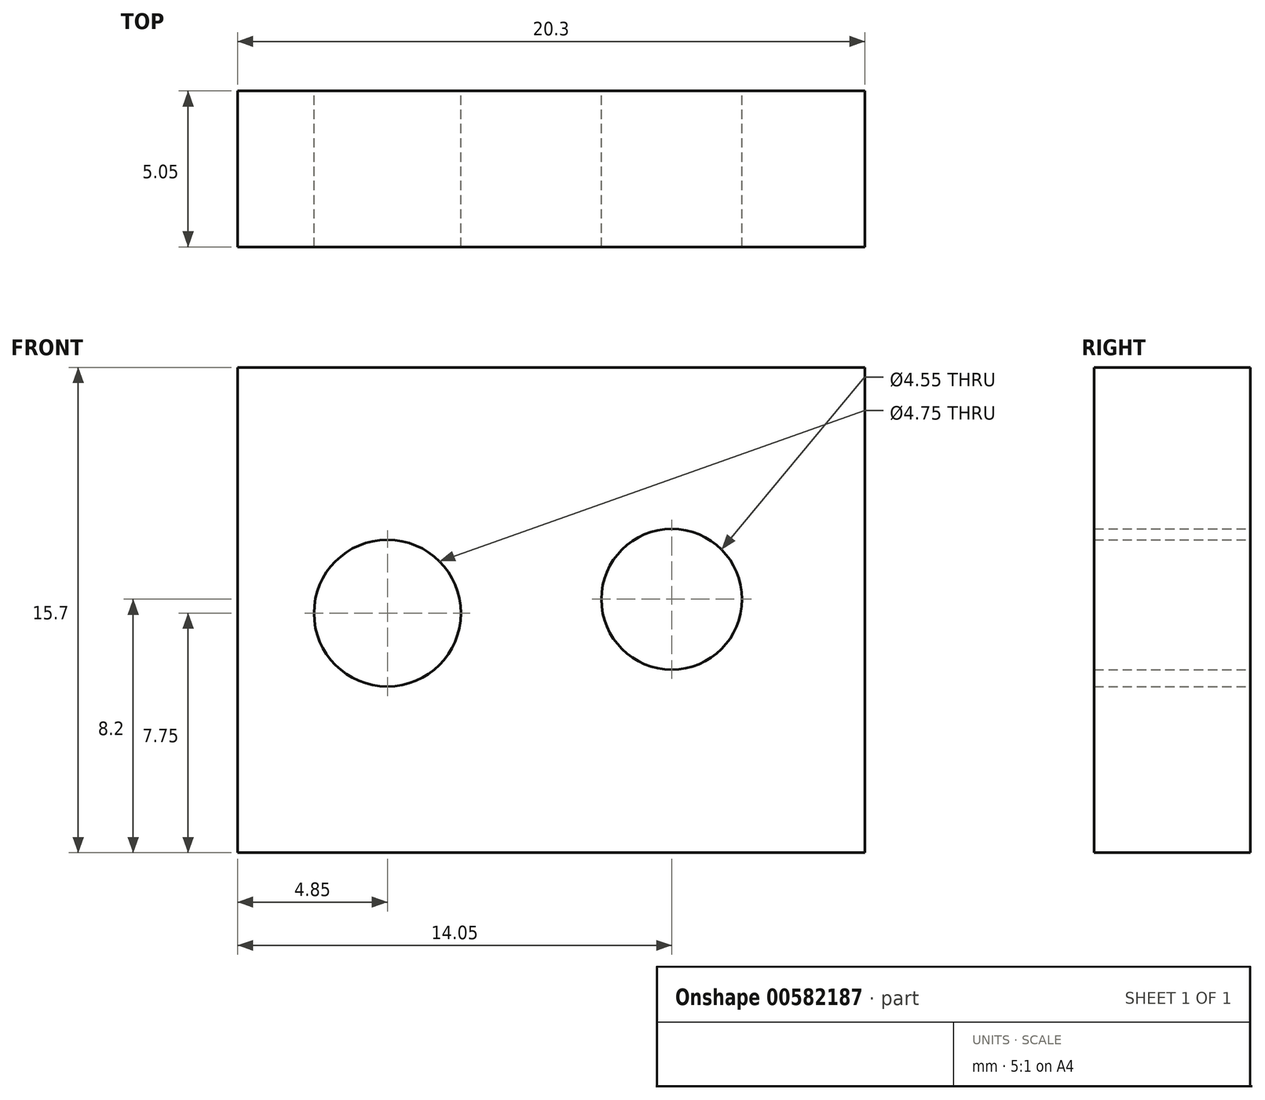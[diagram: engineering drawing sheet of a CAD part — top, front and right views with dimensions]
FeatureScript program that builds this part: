
annotation { "Feature Type Name" : "Feature", "Feature Type Description" : "" }
export const myFeature = defineFeature(function(context is Context, id is Id, definition is map)
    precondition{}
    {
        {
            var Q0;
            Q0=qCreatedBy(makeId("Front.planeOp"),FACE);
            var sketch = newSketch(context, id + "F0", { "sketchPlane" : qUnion([Q0])});
            skLineSegment(sketch, "E0.bottom", {"start": v(10.15, -7.85) * mm, "end": v(-10.15, -7.85) * mm});
            skLineSegment(sketch, "E0.top", {"start": v(10.15, 7.85) * mm, "end": v(-10.15, 7.85) * mm});
            skLineSegment(sketch, "E0.left", {"start": v(10.15, -7.85) * mm, "end": v(10.15, 7.85) * mm});
            skLineSegment(sketch, "E0.right", {"start": v(-10.15, -7.85) * mm, "end": v(-10.15, 7.85) * mm});
            skPoint(sketch, "E0.middle", {"position": v(0, 0) * mm});
            skCircle(sketch, "E1", {"center": v(3.9, 0.35) * mm, "radius": 2.27 * mm});
            skCircle(sketch, "E2", {"center": v(-5.3, -0.1) * mm, "radius": 2.38 * mm});
            skSolve(sketch);
        }
        {
            var Q0;
            Q0=makeQuery(id+"F0.imprint","IMPRINT",FACE,{"disambiguationData":[TD([[makeQuery(id+"F0.imprint","IMPRINT",EDGE,{"derivedFrom":sQuery(id+"F0.wireOp",EDGE,"E0.bottom")}),-1.0]])]});
            extrude(context, id + "F1", {"entities" : qUnion([Q0]), "depth" : 5.05 * mm, "offsetDistance" : 25 * mm});
        }
    });
